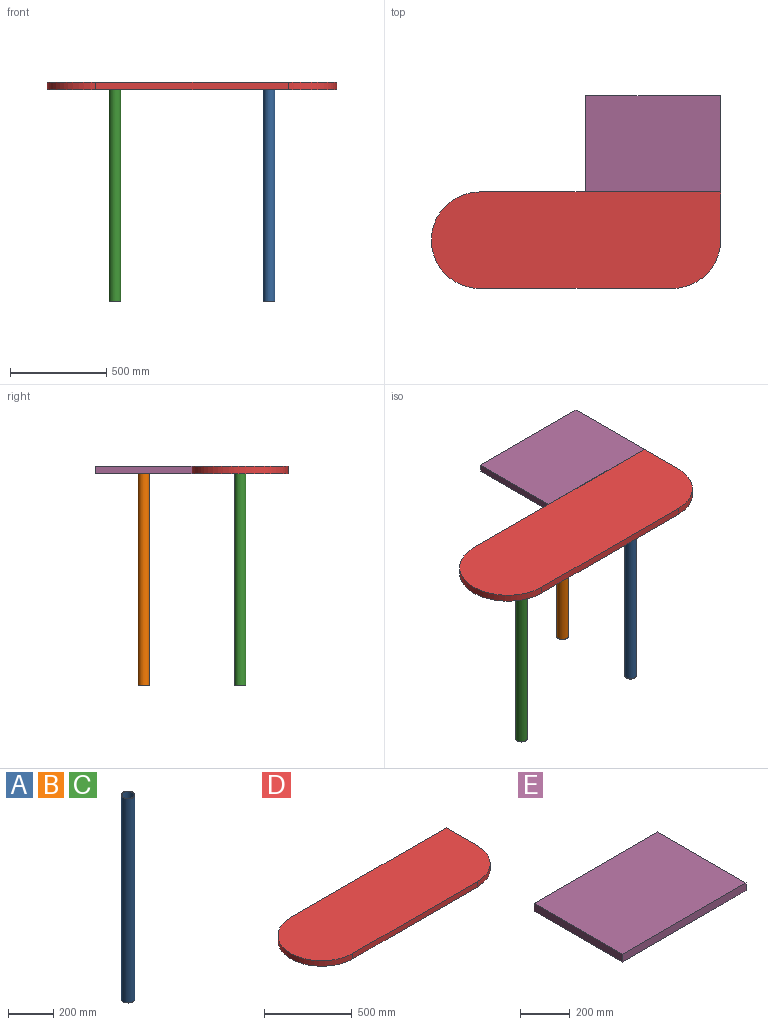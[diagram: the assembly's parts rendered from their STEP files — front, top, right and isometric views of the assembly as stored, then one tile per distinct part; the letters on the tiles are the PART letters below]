
ASSEMBLY  parts=5 mates=3
PART A: 4 faces, bbox 60x60x1100 mm
  f0: plane 60x60mm, normal (0,0,1), area 537.2mm2, adj f2,f3
  f1: plane 60x60mm, normal (0,0,-1), area 537.2mm2, adj f2,f3
  f2: cylinder r=30mm len=1100mm, axis (0,0,1), area 207345.1mm2, adj f0,f1
  f3: cylinder r=27mm len=1100mm, axis (0,0,1), area 186610.6mm2, adj f0,f1
PART B: same geometry as A
PART C: same geometry as A
PART D: 7 faces, bbox 1500x500x38 mm
  f0: plane 1250x38mm, normal (0,1,0), area 47500mm2, adj f1,f4,f5,f6
  f1: cylinder r=250mm len=500mm, axis (0,0,-1), area 29845.1mm2, adj f0,f2,f5,f6
  f2: plane 1000x38mm, normal (0,-1,0), area 38000mm2, adj f1,f3,f5,f6
  f3: cylinder r=250mm len=250mm, axis (0,0,-1), area 14922.6mm2, adj f2,f4,f5,f6
  f4: plane 250x38mm, normal (1,0,0), area 9500mm2, adj f0,f3,f5,f6
  f5: plane 1500x500mm, normal (0,0,1), area 709762.2mm2, adj f0,f1,f2,f3,f4
  f6: plane 1500x500mm, normal (0,0,-1), area 709762.2mm2, adj f0,f1,f2,f3,f4
PART E: 6 faces, bbox 700x500x38 mm
  f0: plane 700x38mm, normal (0,1,0), area 26600mm2, adj f1,f3,f4,f5
  f1: plane 500x38mm, normal (-1,0,0), area 19000mm2, adj f0,f2,f4,f5
  f2: plane 700x38mm, normal (0,-1,0), area 26600mm2, adj f1,f3,f4,f5
  f3: plane 500x38mm, normal (1,0,0), area 19000mm2, adj f0,f2,f4,f5
  f4: plane 700x500mm, normal (0,0,1), area 350000mm2, adj f0,f1,f2,f3
  f5: plane 700x500mm, normal (0,0,-1), area 350000mm2, adj f0,f1,f2,f3
PLACE A t=(-1337.82,-781.35,-209.75)mm
PLACE B t=(-1337.82,-281.35,-209.75)mm
PLACE C t=(-2137.82,-781.35,-209.75)mm
PLACE D t=(-462.58,-151.38,314.89)mm fixed
PLACE E t=(-462.58,-151.38,314.89)mm fixed
MATE fastened C.f2 <-> D.f6  axis (0,0,1) through (-1971.13,-781.35,314.89)mm
MATE fastened B.f2 <-> E.f5  axis (0,0,1) through (-1171.13,-281.35,314.89)mm
MATE fastened A.f2 <-> D.f6  axis (0,0,1) through (-1171.13,-781.35,314.89)mm
